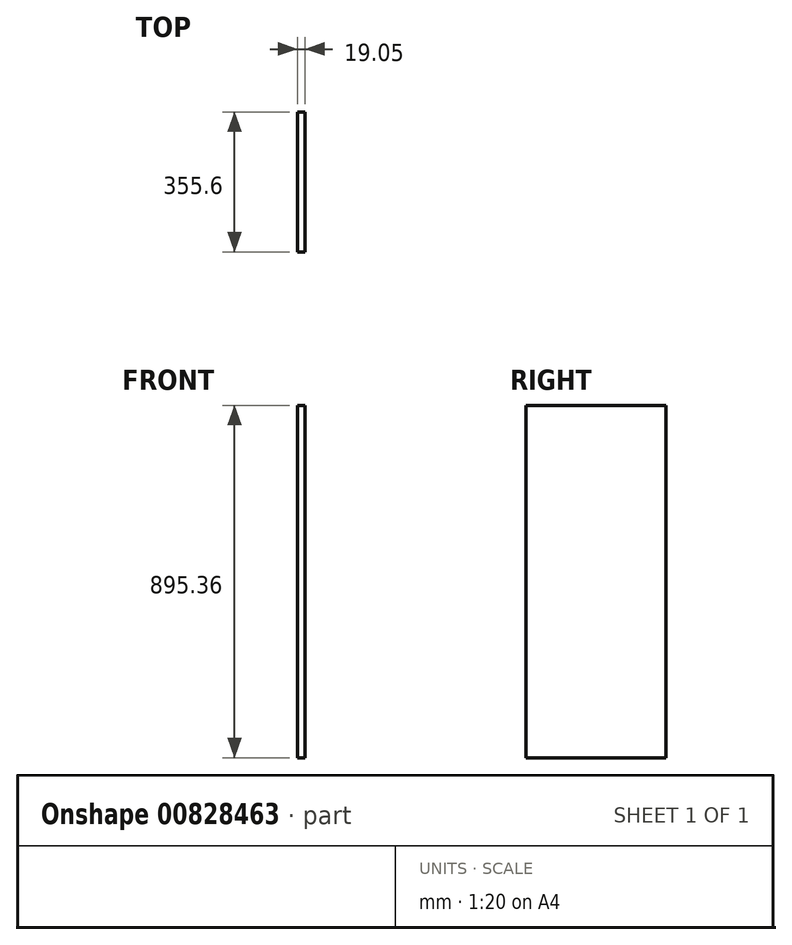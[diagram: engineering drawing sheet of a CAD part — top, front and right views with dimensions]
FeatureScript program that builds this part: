
annotation { "Feature Type Name" : "Feature", "Feature Type Description" : "" }
export const myFeature = defineFeature(function(context is Context, id is Id, definition is map)
    precondition{}
    {
        {
            var Q0;
            Q0=qCreatedBy(makeId("Right.planeOp"),FACE);
            var sketch = newSketch(context, id + "F0", { "sketchPlane" : qUnion([Q0])});
            skLineSegment(sketch, "E0.bottom", {"start": v(177.8, 447.68) * mm, "end": v(-177.8, 447.68) * mm});
            skLineSegment(sketch, "E0.top", {"start": v(177.8, -447.68) * mm, "end": v(-177.8, -447.68) * mm});
            skLineSegment(sketch, "E0.left", {"start": v(177.8, 447.68) * mm, "end": v(177.8, -447.68) * mm});
            skLineSegment(sketch, "E0.right", {"start": v(-177.8, 447.68) * mm, "end": v(-177.8, -447.68) * mm});
            skPoint(sketch, "E0.middle", {"position": v(0, 0) * mm});
            skSolve(sketch);
        }
        {
            var Q0;
            Q0=makeQuery(id+"F0.imprint","IMPRINT",FACE,{"disambiguationData":[TD([[makeQuery(id+"F0.imprint","IMPRINT",EDGE,{"derivedFrom":sQuery(id+"F0.wireOp",EDGE,"E0.bottom")}),1.0]])]});
            extrude(context, id + "F1", {"entities" : qUnion([Q0]), "depth" : 19.05 * mm, "offsetDistance" : 25.4 * mm});
        }
    });
